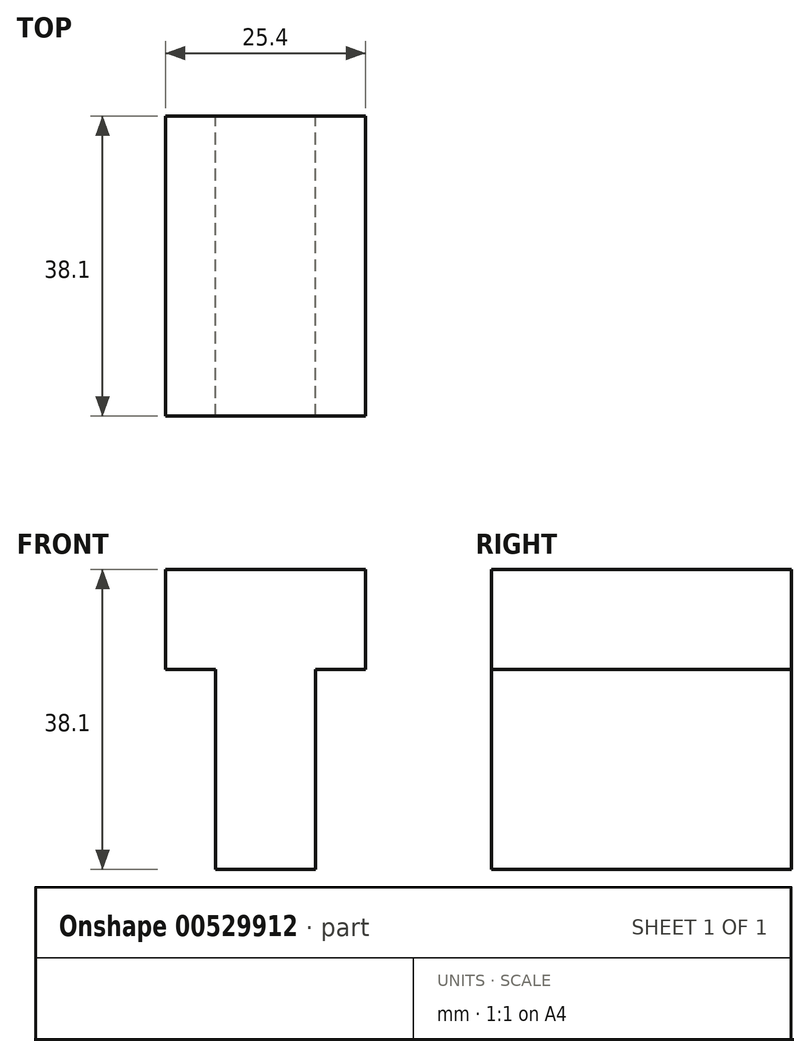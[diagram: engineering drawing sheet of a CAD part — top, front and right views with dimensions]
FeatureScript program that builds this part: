
annotation { "Feature Type Name" : "Feature", "Feature Type Description" : "" }
export const myFeature = defineFeature(function(context is Context, id is Id, definition is map)
    precondition{}
    {
        {
            var Q0;
            Q0=qCreatedBy(makeId("Front.planeOp"),FACE);
            var sketch = newSketch(context, id + "F0", { "sketchPlane" : qUnion([Q0])});
            skLineSegment(sketch, "E0", {"start": v(-58.74, 44.58) * mm, "end": v(-33.34, 44.58) * mm});
            skLineSegment(sketch, "E1", {"start": v(-58.74, 44.58) * mm, "end": v(-58.74, 31.88) * mm});
            skLineSegment(sketch, "E2", {"start": v(-33.34, 44.58) * mm, "end": v(-33.34, 31.88) * mm});
            skLineSegment(sketch, "E3", {"start": v(-58.74, 31.88) * mm, "end": v(-52.39, 31.88) * mm});
            skLineSegment(sketch, "E4", {"start": v(-33.34, 31.88) * mm, "end": v(-39.69, 31.88) * mm});
            skLineSegment(sketch, "E5", {"start": v(-52.39, 31.88) * mm, "end": v(-52.39, 6.48) * mm});
            skLineSegment(sketch, "E6", {"start": v(-39.69, 31.88) * mm, "end": v(-39.69, 6.48) * mm});
            skLineSegment(sketch, "E7", {"start": v(-52.39, 6.48) * mm, "end": v(-39.69, 6.48) * mm});
            skSolve(sketch);
        }
        {
            var Q0;
            Q0 = qSketchRegion(id + "F0", true);
            extrude(context, id + "F1", {"entities" : qUnion([Q0]), "depth" : 38.1 * mm, "offsetDistance" : 25.4 * mm});
        }
    });
